# Revit family: NC0118000
name_source: partatom
category: Plumbing Fixtures
revit_build: Autodesk Revit 2016 (Build: 20150220_1215(x64)
units: mm (PartAtom-declared; Revit-internal decimal feet)

## family parameters
Always vertical = Yes
Cut with Voids When Loaded = No
OmniClass Number = 23.45.00.00
OmniClass Title = Sanitary, Laundry, and Cleaning Equipment
Part Type = Normal
Room Calculation Point = No
Round Connector Dimension = Use Diameter
Shared = No
Work Plane-Based = No

## types (1)
- 610 x 510 x 250
    Assembly Code = D2010400
    CW Connection = Yes
    Depth = 242 mm  [stored 0.793963 ft]
    Description = Fregadero encimera GUTEN, de una cubeta, sin rebalse, para
instalación en encimera para cubiertas de
mínimo 60 cm, Orificio para grifería monomando, Acero inoxidable 18/10 Cromo Níquel
espesor de 1 mm
    HW Connection = Yes
    Height = 900 mm
    Manufacturer = CHC
    Material = Stainless Steel, Polished
    Model = NC0118000
    Type Image = NC0118000.jpg
    URL = www.grupochc.cl
    Vent Connection = No
    Waste Connection = Yes

note: [stored X ft] marks values corroborated as IEEE doubles in the binary element streams (Revit-internal decimal feet)

## geometry (parser evidence)
native form markers: Sweep x2
no freeform markers — native parametric forms only
